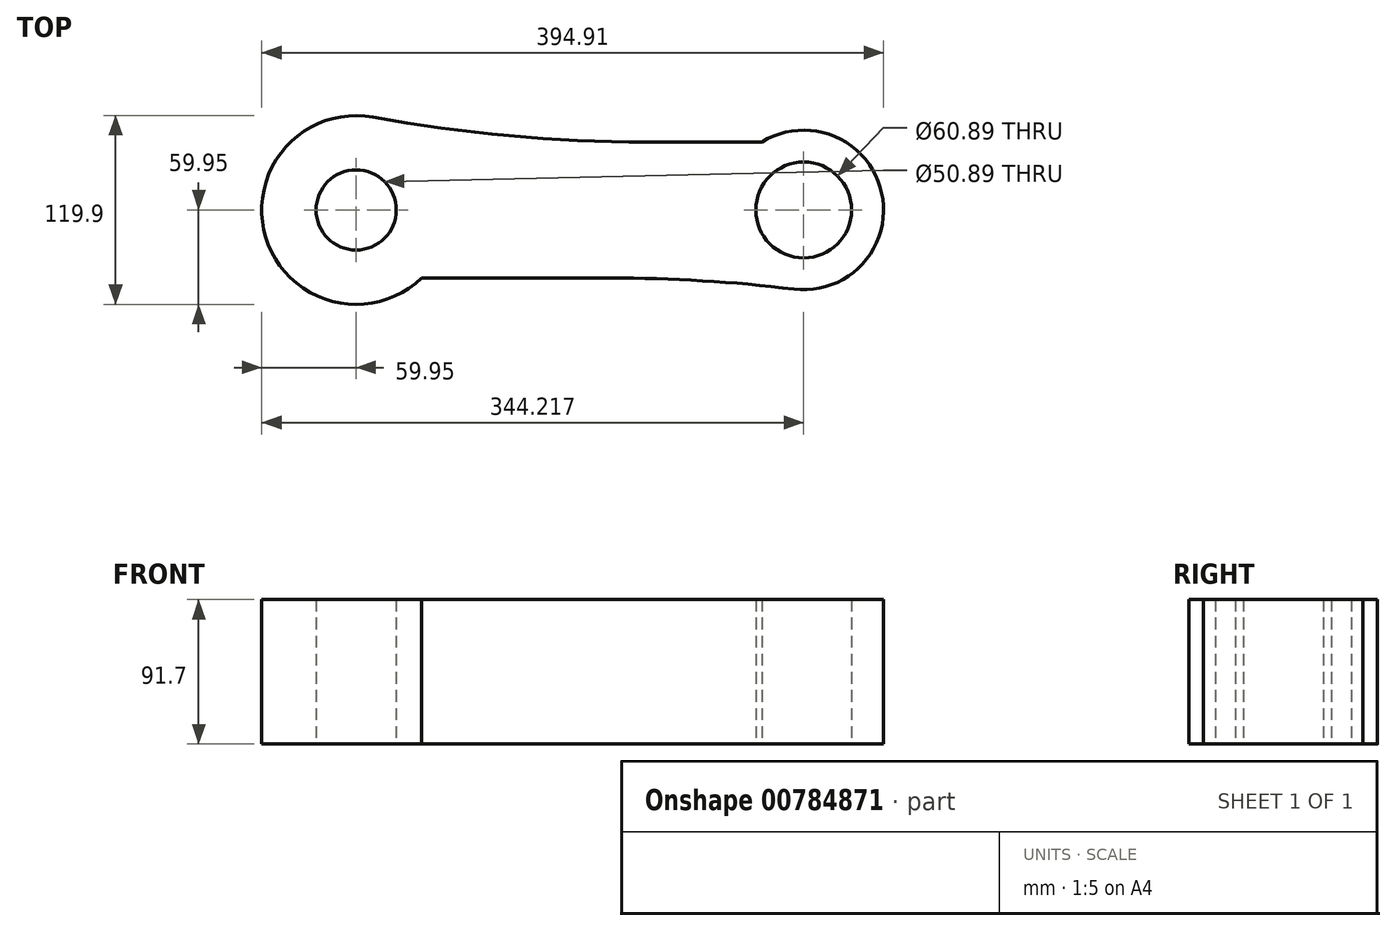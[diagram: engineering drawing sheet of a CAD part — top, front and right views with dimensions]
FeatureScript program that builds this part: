
annotation { "Feature Type Name" : "Feature", "Feature Type Description" : "" }
export const myFeature = defineFeature(function(context is Context, id is Id, definition is map)
    precondition{}
    {
        {
            var Q0;
            Q0=qCreatedBy(makeId("Top.planeOp"),FACE);
            var sketch = newSketch(context, id + "F0", { "sketchPlane" : qUnion([Q0])});
            skCircle(sketch, "E0", {"center": v(0, 0) * mm, "radius": 59.95 * mm});
            skCircle(sketch, "E1", {"center": v(0, 0) * mm, "radius": 25.44 * mm});
            skCircle(sketch, "E2", {"center": v(284.27, 0) * mm, "radius": 30.45 * mm});
            skCircle(sketch, "E3", {"center": v(284.27, 0) * mm, "radius": 50.7 * mm});
            skLineSegment(sketch, "E4", {"start": v(41.57, 43.2) * mm, "end": v(257.75, 43.2) * mm});
            skLineSegment(sketch, "E5", {"start": v(0, 0) * mm, "end": v(284.27, 0) * mm});
            skLineSegment(sketch, "E6.MirrorCS", {"start": v(41.57, -43.2) * mm, "end": v(257.75, -43.2) * mm});
            skSolve(sketch);
        }
        {
            var Q0;
            {var subQ0=sQuery(id+"F0.wireOp",EDGE,"E4");Q0=makeQuery(id+"F0.imprint","IMPRINT",FACE,{"disambiguationData":[TD([[makeQuery(id+"F0.imprint","IMPRINT",EDGE,{"derivedFrom":subQ0}),-1.0]])]});}
            var Q1;
            Q1=makeQuery(id+"F0.imprint","IMPRINT",FACE,{"disambiguationData":[TD([[makeQuery(id+"F0.imprint","IMPRINT",EDGE,{"derivedFrom":sQuery(id+"F0.wireOp",EDGE,"E2")}),-1.0]])]});
            var Q2;
            {var subQ0=sQuery(id+"F0.wireOp",EDGE,"E6.MirrorCS");Q2=makeQuery(id+"F0.imprint","IMPRINT",FACE,{"disambiguationData":[TD([[makeQuery(id+"F0.imprint","IMPRINT",EDGE,{"derivedFrom":subQ0}),1.0]])]});}
            var Q3;
            Q3=makeQuery(id+"F0.imprint","IMPRINT",FACE,{"disambiguationData":[TD([[makeQuery(id+"F0.imprint","IMPRINT",EDGE,{"derivedFrom":sQuery(id+"F0.wireOp",EDGE,"E1")}),-1.0]])]});
            extrude(context, id + "F1", {"entities" : qUnion([Q0, Q1, Q2, Q3]), "depth" : 91.7 * mm, "offsetDistance" : 25.4 * mm});
        }
        {
            var Q0;
            Q0=makeQuery(id+"F1.opExtrude","SWEPT_EDGE",EDGE,{"disambiguationData":[OSD([sQuery(id+"F0.wireOp",EDGE,"E3"),sQuery(id+"F0.wireOp",EDGE,"E6.MirrorCS")])]});
            var Q1;
            Q1=makeQuery(id+"F1.opExtrude","SWEPT_EDGE",EDGE,{"disambiguationData":[OSD([sQuery(id+"F0.wireOp",EDGE,"E0"),sQuery(id+"F0.wireOp",EDGE,"E4")])]});
            fillet(context, id + "F2", {"entities" : qUnion([Q0, Q1]), "radius" : 960 * mm, "tangentPropagation" : true, "allowEdgeOverflow" : false});
        }
    });
